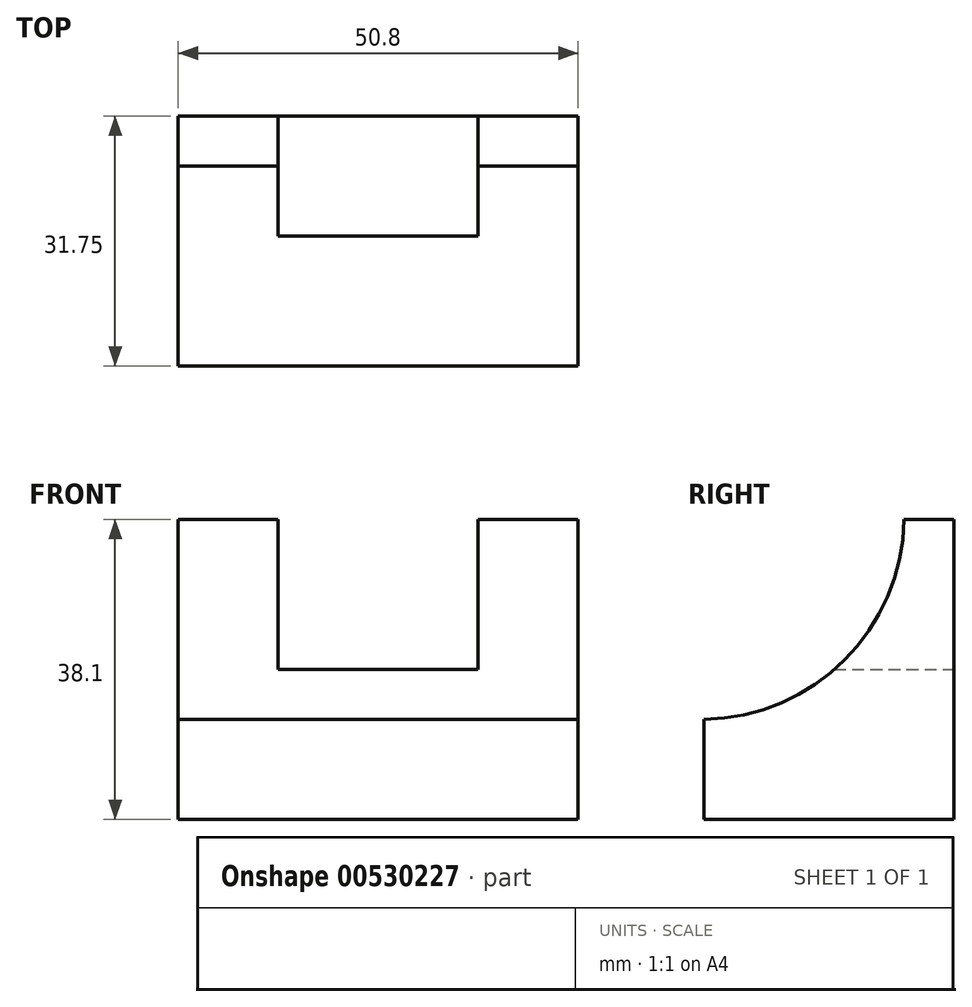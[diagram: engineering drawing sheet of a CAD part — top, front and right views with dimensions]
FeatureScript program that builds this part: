
annotation { "Feature Type Name" : "Feature", "Feature Type Description" : "" }
export const myFeature = defineFeature(function(context is Context, id is Id, definition is map)
    precondition{}
    {
        {
            var Q0;
            Q0=qCreatedBy(makeId("Front.planeOp"),FACE);
            var sketch = newSketch(context, id + "F0", { "sketchPlane" : qUnion([Q0])});
            skLineSegment(sketch, "E0", {"start": v(0, 0) * mm, "end": v(-50.8, 0) * mm});
            skLineSegment(sketch, "E1", {"start": v(-50.8, 0) * mm, "end": v(-50.8, 38.1) * mm});
            skLineSegment(sketch, "E2", {"start": v(-50.8, 38.1) * mm, "end": v(0, 38.1) * mm});
            skLineSegment(sketch, "E3", {"start": v(0, 38.1) * mm, "end": v(0, 0) * mm});
            skSolve(sketch);
        }
        {
            var Q0;
            Q0 = qSketchRegion(id + "F0", true);
            var Q1;
            Q1=makeQuery(id+"F0.imprint","IMPRINT",FACE,{"disambiguationData":[TD([[makeQuery(id+"F0.imprint","IMPRINT",EDGE,{"derivedFrom":sQuery(id+"F0.wireOp",EDGE,"E0")}),-1.0]])]});
            extrude(context, id + "F1", {"entities" : qUnion([Q0, Q1]), "depth" : 31.75 * mm, "offsetDistance" : 25.4 * mm});
        }
        {
            var Q0;
            Q0=makeQuery(id+"F1.opExtrude","SWEPT_FACE",FACE,{"disambiguationData":[OSD([sQuery(id+"F0.wireOp",EDGE,"E3")])]});
            var sketch = newSketch(context, id + "F2", { "sketchPlane" : qUnion([Q0])});
            skArc(sketch, "E4", {"start": v(-31.75, 12.7) * mm, "mid": v(-13.92, 20.27) * mm, "end": v(-6.35, 38.1) * mm});
            skSolve(sketch);
        }
        {
            var Q0;
            Q0 = qSketchRegion(id + "F2", true);
            var Q1;
            {var subQ0=sQuery(id+"F2.wireOp",EDGE,"E4");Q1=makeQuery(id+"F2.imprint","IMPRINT",FACE,{"disambiguationData":[TD([[makeQuery(id+"F2.imprint","IMPRINT",EDGE,{"derivedFrom":subQ0}),1.0]])]});}
            extrude(context, id + "F3", {"entities" : qUnion([Q0, Q1]), "operationType" : NewBodyOperationType.REMOVE, "endBound" : BoundingType.THROUGH_ALL, "oppositeDirection" : true, "depth" : 25.4 * mm, "offsetDistance" : 25.4 * mm});
        }
        {
            var Q0;
            Q0=makeQuery(id+"F1.opExtrude","CAP_FACE",FACE,{"disambiguationData":[OSD([sQuery(id+"F0.wireOp",EDGE,"E0"),sQuery(id+"F0.wireOp",EDGE,"E1"),sQuery(id+"F0.wireOp",EDGE,"E2"),sQuery(id+"F0.wireOp",EDGE,"E3")])],"isStart":true});
            var sketch = newSketch(context, id + "F4", { "sketchPlane" : qUnion([Q0])});
            skLineSegment(sketch, "E5", {"start": v(12.7, 38.1) * mm, "end": v(12.7, 19.05) * mm});
            skLineSegment(sketch, "E6", {"start": v(12.7, 19.05) * mm, "end": v(38.1, 19.05) * mm});
            skLineSegment(sketch, "E7", {"start": v(38.1, 19.05) * mm, "end": v(38.1, 38.1) * mm});
            skSolve(sketch);
        }
        {
            var Q0;
            Q0 = qSketchRegion(id + "F4", true);
            var Q1;
            {var subQ0=sQuery(id+"F4.wireOp",EDGE,"E5");Q1=makeQuery(id+"F4.imprint","IMPRINT",FACE,{"disambiguationData":[TD([[makeQuery(id+"F4.imprint","IMPRINT",EDGE,{"derivedFrom":subQ0}),1.0]])]});}
            extrude(context, id + "F5", {"entities" : qUnion([Q0, Q1]), "operationType" : NewBodyOperationType.REMOVE, "oppositeDirection" : true, "depth" : 25.4 * mm, "offsetDistance" : 25.4 * mm});
        }
    });
